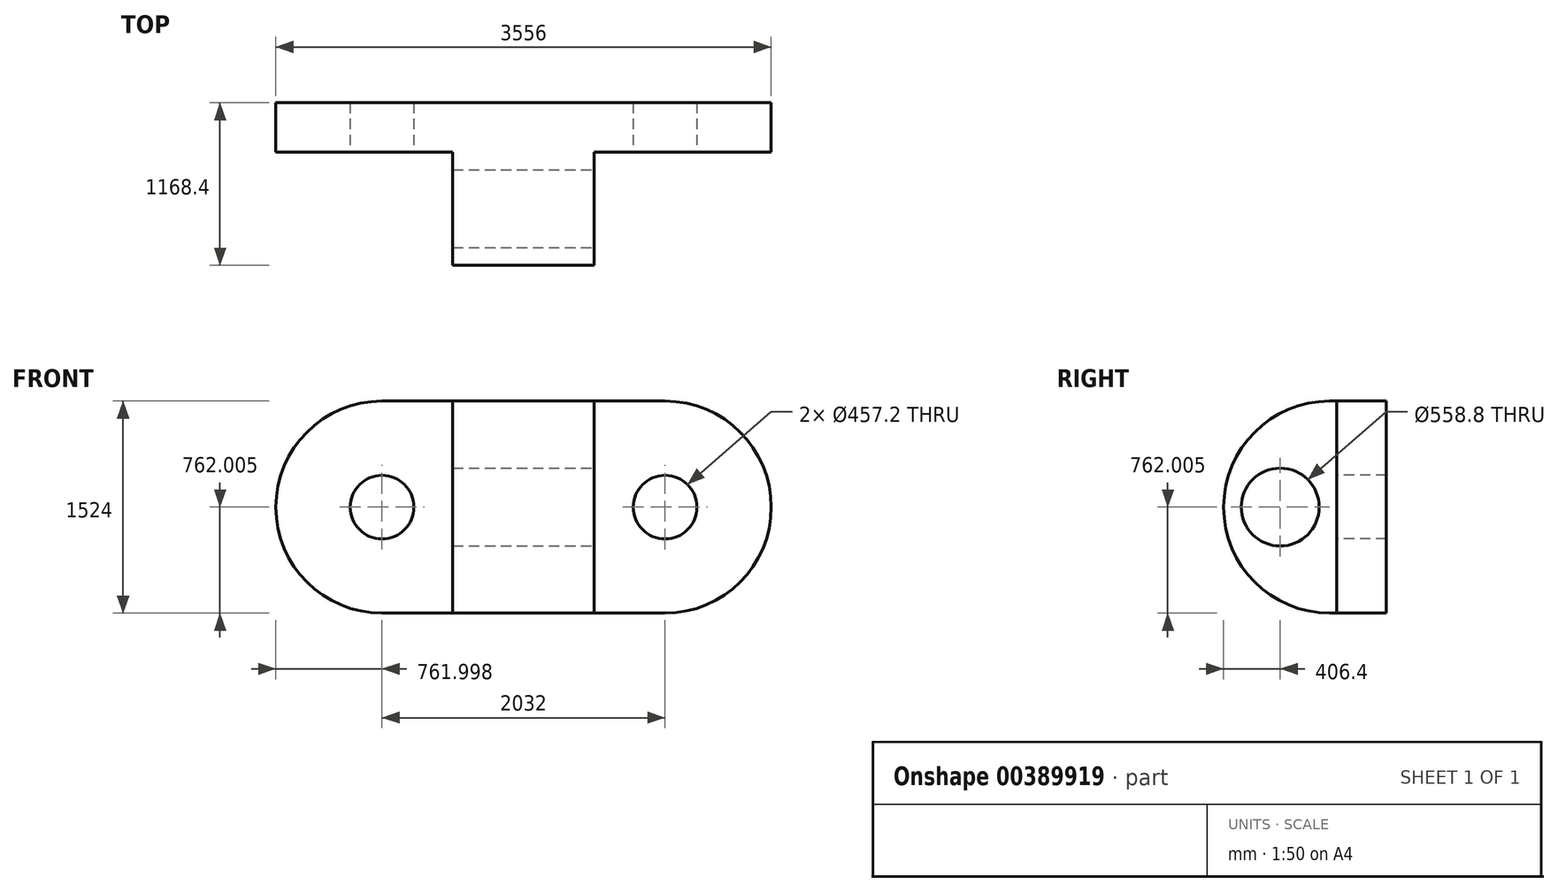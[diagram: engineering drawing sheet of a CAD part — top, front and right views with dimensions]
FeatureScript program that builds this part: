
annotation { "Feature Type Name" : "Feature", "Feature Type Description" : "" }
export const myFeature = defineFeature(function(context is Context, id is Id, definition is map)
    precondition{}
    {
        {
            var Q0;
            Q0=qCreatedBy(makeId("Front.planeOp"),FACE);
            var sketch = newSketch(context, id + "F0", { "sketchPlane" : qUnion([Q0])});
            skLineSegment(sketch, "E0.bottom", {"start": v(-1767.46, 504.06) * mm, "end": v(1788.54, 504.06) * mm});
            skLineSegment(sketch, "E0.top", {"start": v(-1767.46, -1019.94) * mm, "end": v(1788.54, -1019.94) * mm});
            skLineSegment(sketch, "E0.left", {"start": v(-1767.46, 504.06) * mm, "end": v(-1767.46, -1019.94) * mm});
            skLineSegment(sketch, "E0.right", {"start": v(1788.54, 504.06) * mm, "end": v(1788.54, -1019.94) * mm});
            skSolve(sketch);
        }
        {
            var Q0;
            Q0 = qSketchRegion(id + "F0", true);
            extrude(context, id + "F1", {"entities" : qUnion([Q0]), "depth" : 1168.4 * mm});
        }
        {
            var Q0;
            Q0=makeQuery(id+"F1.opExtrude","CAP_FACE",FACE,{"disambiguationData":[OSD([sQuery(id+"F0.wireOp",EDGE,"E0.bottom"),sQuery(id+"F0.wireOp",EDGE,"E0.top"),sQuery(id+"F0.wireOp",EDGE,"E0.left"),sQuery(id+"F0.wireOp",EDGE,"E0.right")])],"isStart":false});
            var sketch = newSketch(context, id + "F2", { "sketchPlane" : qUnion([Q0])});
            skLineSegment(sketch, "E1.bottom", {"start": v(-2002.89, 827.87) * mm, "end": v(-497.46, 827.87) * mm});
            skLineSegment(sketch, "E1.top", {"start": v(-2002.89, -1240.08) * mm, "end": v(-497.46, -1240.08) * mm});
            skLineSegment(sketch, "E1.left", {"start": v(-2002.89, 827.87) * mm, "end": v(-2002.89, -1240.08) * mm});
            skLineSegment(sketch, "E1.right", {"start": v(-497.46, 827.87) * mm, "end": v(-497.46, -1240.08) * mm});
            skSolve(sketch);
        }
        {
            var Q0;
            Q0 = qSketchRegion(id + "F2", true);
            extrude(context, id + "F3", {"entities" : qUnion([Q0]), "operationType" : NewBodyOperationType.REMOVE, "oppositeDirection" : true, "depth" : 812.8 * mm});
        }
        {
            var Q0;
            Q0=makeQuery(id+"F1.opExtrude","CAP_FACE",FACE,{"disambiguationData":[OSD([sQuery(id+"F0.wireOp",EDGE,"E0.bottom"),sQuery(id+"F0.wireOp",EDGE,"E0.top"),sQuery(id+"F0.wireOp",EDGE,"E0.left"),sQuery(id+"F0.wireOp",EDGE,"E0.right")])],"isStart":false});
            var sketch = newSketch(context, id + "F4", { "sketchPlane" : qUnion([Q0])});
            skLineSegment(sketch, "E2.bottom", {"start": v(518.54, 1433.37) * mm, "end": v(2227.43, 1433.37) * mm});
            skLineSegment(sketch, "E2.top", {"start": v(518.54, -2141) * mm, "end": v(2227.43, -2141) * mm});
            skLineSegment(sketch, "E2.left", {"start": v(518.54, 1433.37) * mm, "end": v(518.54, -2141) * mm});
            skLineSegment(sketch, "E2.right", {"start": v(2227.43, 1433.37) * mm, "end": v(2227.43, -2141) * mm});
            skSolve(sketch);
        }
        {
            var Q0;
            Q0 = qSketchRegion(id + "F4", true);
            extrude(context, id + "F5", {"entities" : qUnion([Q0]), "operationType" : NewBodyOperationType.REMOVE, "oppositeDirection" : true, "depth" : 812.8 * mm});
        }
        {
            var Q0;
            Q0=makeQuery(id+"F1.opExtrude","CAP_EDGE",EDGE,{"disambiguationData":[OSD([sQuery(id+"F0.wireOp",EDGE,"E0.bottom")])],"isStart":false});
            var Q1;
            Q1=makeQuery(id+"F1.opExtrude","CAP_EDGE",EDGE,{"disambiguationData":[OSD([sQuery(id+"F0.wireOp",EDGE,"E0.top")])],"isStart":false});
            fillet(context, id + "F6", {"entities" : qUnion([Q0, Q1]), "radius" : 762 * mm, "tangentPropagation" : true, "allowEdgeOverflow" : false});
        }
        {
            var Q0;
            Q0=makeQuery(id+"F1.opExtrude","SWEPT_EDGE",EDGE,{"disambiguationData":[OSD([sQuery(id+"F0.wireOp",EDGE,"E0.top"),sQuery(id+"F0.wireOp",EDGE,"E0.right")])]});
            var Q1;
            Q1=makeQuery(id+"F1.opExtrude","SWEPT_EDGE",EDGE,{"disambiguationData":[OSD([sQuery(id+"F0.wireOp",EDGE,"E0.bottom"),sQuery(id+"F0.wireOp",EDGE,"E0.right")])]});
            var Q2;
            Q2=makeQuery(id+"F1.opExtrude","SWEPT_EDGE",EDGE,{"disambiguationData":[OSD([sQuery(id+"F0.wireOp",EDGE,"E0.bottom"),sQuery(id+"F0.wireOp",EDGE,"E0.left")])]});
            var Q3;
            Q3=makeQuery(id+"F1.opExtrude","SWEPT_EDGE",EDGE,{"disambiguationData":[OSD([sQuery(id+"F0.wireOp",EDGE,"E0.top"),sQuery(id+"F0.wireOp",EDGE,"E0.left")])]});
            fillet(context, id + "F7", {"entities" : qUnion([Q0, Q1, Q2, Q3]), "radius" : 762 * mm, "tangentPropagation" : true, "allowEdgeOverflow" : false});
        }
        {
            var Q0;
            Q0=makeQuery(id+"F3.boolean.opBoolean","COPY",FACE,{"derivedFrom":makeQuery(id+"F3.opExtrude","CAP_FACE",FACE,{"disambiguationData":[OSD([sQuery(id+"F2.wireOp",EDGE,"E1.bottom"),sQuery(id+"F2.wireOp",EDGE,"E1.top"),sQuery(id+"F2.wireOp",EDGE,"E1.left"),sQuery(id+"F2.wireOp",EDGE,"E1.right")])],"isStart":false})});
            var sketch = newSketch(context, id + "F8", { "sketchPlane" : qUnion([Q0])});
            skCircle(sketch, "E3", {"center": v(-1005.46, -257.94) * mm, "radius": 228.6 * mm});
            skSolve(sketch);
        }
        {
            var Q0;
            Q0=makeQuery(id+"F5.boolean.opBoolean","COPY",FACE,{"derivedFrom":makeQuery(id+"F5.opExtrude","CAP_FACE",FACE,{"disambiguationData":[OSD([sQuery(id+"F4.wireOp",EDGE,"E2.bottom"),sQuery(id+"F4.wireOp",EDGE,"E2.top"),sQuery(id+"F4.wireOp",EDGE,"E2.left"),sQuery(id+"F4.wireOp",EDGE,"E2.right")])],"isStart":false})});
            var sketch = newSketch(context, id + "F9", { "sketchPlane" : qUnion([Q0])});
            skCircle(sketch, "E4", {"center": v(1026.54, -257.94) * mm, "radius": 228.6 * mm});
            skSolve(sketch);
        }
        {
            var Q0;
            Q0 = qSketchRegion(id + "F9", true);
            extrude(context, id + "F10", {"entities" : qUnion([Q0]), "operationType" : NewBodyOperationType.REMOVE, "endBound" : BoundingType.THROUGH_ALL, "oppositeDirection" : true, "depth" : 25.4 * mm});
        }
        {
            var Q0;
            Q0 = qSketchRegion(id + "F8", true);
            extrude(context, id + "F11", {"entities" : qUnion([Q0]), "operationType" : NewBodyOperationType.REMOVE, "endBound" : BoundingType.THROUGH_ALL, "oppositeDirection" : true, "depth" : 25.4 * mm});
        }
        {
            var Q0;
            Q0=makeQuery(id+"F5.boolean.opBoolean","COPY",FACE,{"derivedFrom":makeQuery(id+"F5.opExtrude","SWEPT_FACE",FACE,{"disambiguationData":[OSD([sQuery(id+"F4.wireOp",EDGE,"E2.left")])]})});
            var sketch = newSketch(context, id + "F12", { "sketchPlane" : qUnion([Q0])});
            skCircle(sketch, "E5", {"center": v(-762, -257.94) * mm, "radius": 279.4 * mm});
            skPoint(sketch, "E5.centerSnap0", {"position": v(-355.6, -257.94) * mm});
            skSolve(sketch);
        }
        {
            var Q0;
            Q0 = qSketchRegion(id + "F12", true);
            extrude(context, id + "F13", {"entities" : qUnion([Q0]), "operationType" : NewBodyOperationType.REMOVE, "endBound" : BoundingType.THROUGH_ALL, "oppositeDirection" : true, "depth" : 25.4 * mm});
        }
    });
